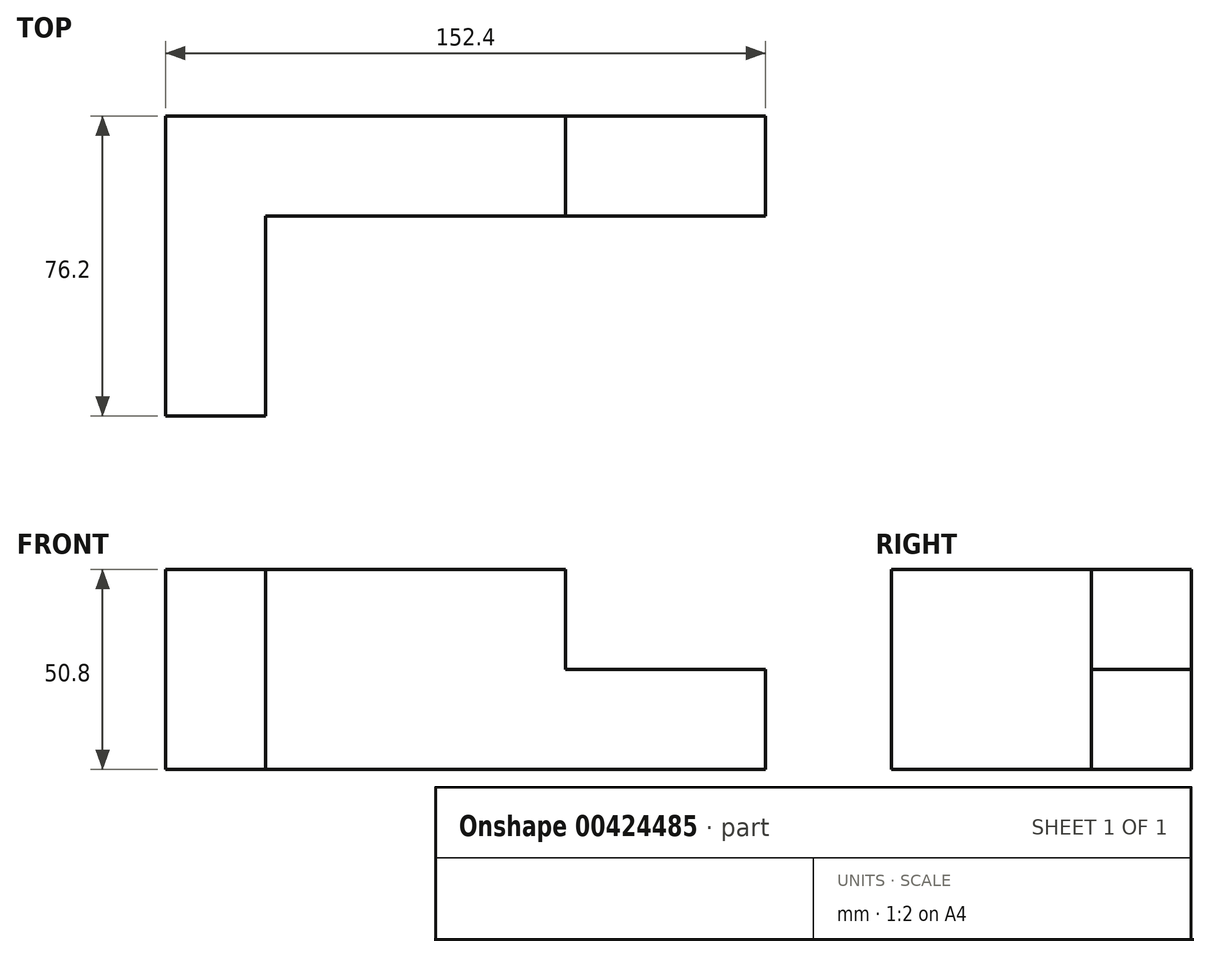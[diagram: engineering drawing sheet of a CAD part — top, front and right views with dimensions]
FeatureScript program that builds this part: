
annotation { "Feature Type Name" : "Feature", "Feature Type Description" : "" }
export const myFeature = defineFeature(function(context is Context, id is Id, definition is map)
    precondition{}
    {
        {
            var Q0;
            Q0=qCreatedBy(makeId("Top.planeOp"),FACE);
            var sketch = newSketch(context, id + "F0", { "sketchPlane" : qUnion([Q0])});
            skLineSegment(sketch, "E0", {"start": v(0, 0) * mm, "end": v(0, 76.2) * mm});
            skLineSegment(sketch, "E1", {"start": v(0, 0) * mm, "end": v(25.4, 0) * mm});
            skLineSegment(sketch, "E2", {"start": v(25.4, 0) * mm, "end": v(25.4, 50.8) * mm});
            skLineSegment(sketch, "E3", {"start": v(25.4, 50.8) * mm, "end": v(152.4, 50.8) * mm});
            skLineSegment(sketch, "E4", {"start": v(0, 76.2) * mm, "end": v(152.4, 76.2) * mm});
            skLineSegment(sketch, "E5", {"start": v(152.4, 50.8) * mm, "end": v(152.4, 76.2) * mm});
            skSolve(sketch);
        }
        {
            var Q0;
            Q0=makeQuery(id+"F0.imprint","IMPRINT",FACE,{"disambiguationData":[TD([[makeQuery(id+"F0.imprint","IMPRINT",EDGE,{"derivedFrom":sQuery(id+"F0.wireOp",EDGE,"E0")}),-1.0]])]});
            extrude(context, id + "F1", {"entities" : qUnion([Q0]), "depth" : 50.8 * mm});
        }
        {
            var Q0;
            Q0=makeQuery(id+"F1.opExtrude","SWEPT_FACE",FACE,{"disambiguationData":[OSD([sQuery(id+"F0.wireOp",EDGE,"E3")])]});
            var sketch = newSketch(context, id + "F2", { "sketchPlane" : qUnion([Q0])});
            skLineSegment(sketch, "E6", {"start": v(152.4, 25.4) * mm, "end": v(101.6, 25.4) * mm});
            skLineSegment(sketch, "E7", {"start": v(101.6, 25.4) * mm, "end": v(101.6, 50.8) * mm});
            skLineSegment(sketch, "E8", {"start": v(101.6, 50.8) * mm, "end": v(152.4, 50.8) * mm});
            skLineSegment(sketch, "E9", {"start": v(152.4, 50.8) * mm, "end": v(152.4, 25.4) * mm});
            skSolve(sketch);
        }
        {
            var Q0;
            Q0=makeQuery(id+"F2.imprint","IMPRINT",FACE,{"disambiguationData":[TD([[makeQuery(id+"F2.imprint","IMPRINT",EDGE,{"derivedFrom":sQuery(id+"F2.wireOp",EDGE,"E6")}),-1.0]])]});
            extrude(context, id + "F3", {"entities" : qUnion([Q0]), "operationType" : NewBodyOperationType.REMOVE, "oppositeDirection" : true, "depth" : 25.4 * mm});
        }
    });
